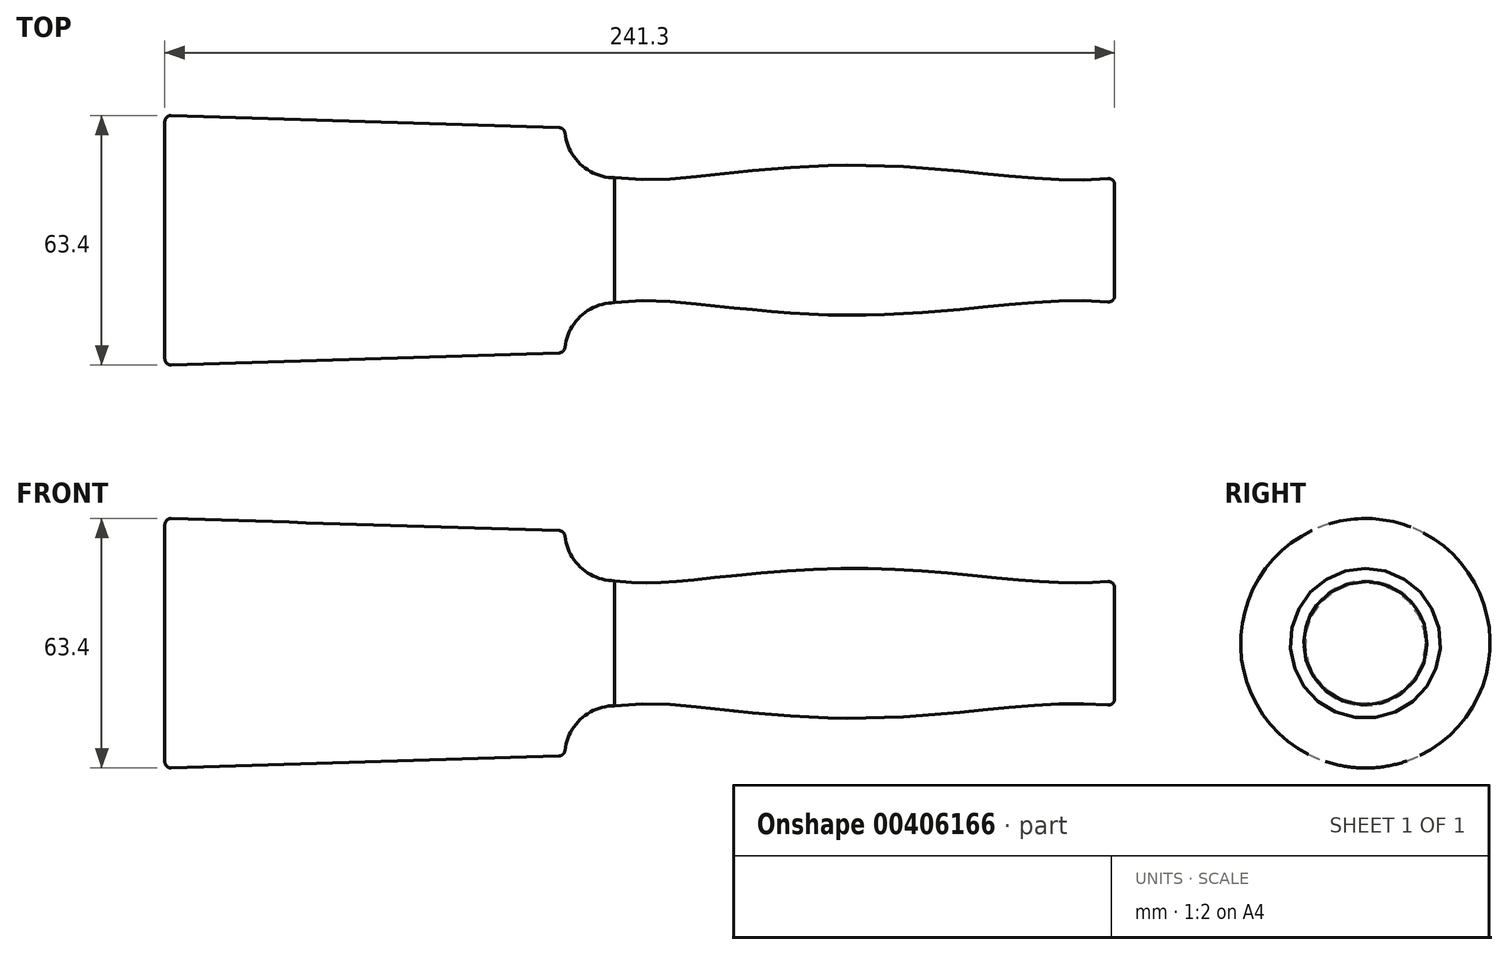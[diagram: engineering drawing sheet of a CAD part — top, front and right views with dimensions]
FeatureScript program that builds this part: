
annotation { "Feature Type Name" : "Feature", "Feature Type Description" : "" }
export const myFeature = defineFeature(function(context is Context, id is Id, definition is map)
    precondition{}
    {
        {
            var Q0;
            Q0=qCreatedBy(makeId("Front.planeOp"),FACE);
            var sketch = newSketch(context, id + "F0", { "sketchPlane" : qUnion([Q0])});
            skLineSegment(sketch, "E0", {"start": v(-101.6, 31.75) * mm, "end": v(0, 28.57) * mm});
            skLineSegment(sketch, "E1", {"start": v(0, 28.58) * mm, "end": v(0, 28.57) * mm});
            skLineSegment(sketch, "E2", {"start": v(-101.6, 0) * mm, "end": v(139.7, 0) * mm});
            skPoint(sketch, "E3.visualSharp", {"position": v(0, 15.87) * mm});
            skArc(sketch, "E4", {"start": v(0, 28.57) * mm, "mid": v(3.72, 19.6) * mm, "end": v(12.7, 15.87) * mm});
            skFitSpline(sketch, "E5", {"points": [v(12.7, 15.87) * mm, v(30.35, 15.87) * mm, v(72.77, 19.05) * mm, v(118.22, 15.87) * mm, v(139.7, 15.87) * mm], "startDerivative": vector(109.4, -12.05) * mm, "endDerivative": vector(87.51, 10.84) * mm});
            skLineSegment(sketch, "E6", {"start": v(-101.6, 31.75) * mm, "end": v(-101.6, 0) * mm});
            skLineSegment(sketch, "E7", {"start": v(139.7, 15.87) * mm, "end": v(139.7, 0) * mm});
            skSolve(sketch);
        }
        {
            var Q0;
            Q0 = qSketchRegion(id + "F0", true);
            var Q1;
            Q1=sQuery(id+"F0.wireOp",EDGE,"E2");
            revolve(context, id + "F1", {"entities" : qUnion([Q0]), "axis" : qUnion([Q1]), "revolveType" : RevolveType.FULL});
        }
        {
            var Q0;
            Q0=makeQuery(id+"F1.opRevolve","SWEPT_EDGE",EDGE,{"disambiguationData":[OSD([sQuery(id+"F0.wireOp",EDGE,"E0"),sQuery(id+"F0.wireOp",EDGE,"E6")])]});
            var Q1;
            Q1=makeQuery(id+"F1.opRevolve","SWEPT_EDGE",EDGE,{"disambiguationData":[OSD([sQuery(id+"F0.wireOp",EDGE,"E0"),sQuery(id+"F0.wireOp",EDGE,"E4")])]});
            var Q2;
            Q2=makeQuery(id+"F1.opRevolve","SWEPT_EDGE",EDGE,{"disambiguationData":[OSD([sQuery(id+"F0.wireOp",EDGE,"E5"),sQuery(id+"F0.wireOp",EDGE,"E7")])]});
            fillet(context, id + "F2", {"entities" : qUnion([Q0, Q1, Q2]), "radius" : 1.59 * mm, "tangentPropagation" : true, "allowEdgeOverflow" : false});
        }
    });
